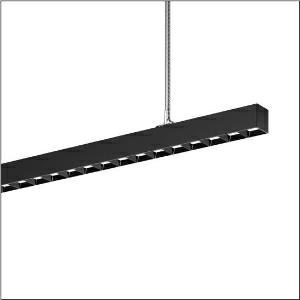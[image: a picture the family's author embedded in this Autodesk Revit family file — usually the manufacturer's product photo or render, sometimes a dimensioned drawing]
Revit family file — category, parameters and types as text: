
# Revit family: silica_r__21_51mx32dc3dbb_53cb
name_source: partatom
category: Lighting Fixtures
units: mm (PartAtom-declared; Revit-internal decimal feet)

## family parameters
Cut with Voids When Loaded = No
Host = Face
Light Source = No
Part Type = Normal
Room Calculation Point = No
Round Connector Dimension = Use Diameter
Shared = No

## types (1)
- --- (1 x LED, 18220 lm, 113 W, 3000K)
    Apparent Load = 113 VA
    CIE Flux Codes = 86 99 100 59 100
    Color Rendering = 80
    Color Temperature = 3000K
    Default Elevation = 1800 mm
    Description = Silica® 21, office luminaire, primary light control with darklight reflector, of PMMA, black, CAT 2 (L<= 3000cd/m²), light emission: direct/indirect distribution, primary light characteristic: symmetric, installation type: suspended mounting, LED, rated luminous flux: 18.220lm, luminous efficacy: 161lm/W, light colour: 830, colour temperature: 3000K, with terminal, 3+2-pole, max. 2.5mm², mains connection: 220..240V, AC, 50/60Hz, rated input power: 113W, luminaire housing, of aluminium, jet black (RAL 9005), length: 3.004mm, width: 53mm, height: 53mm, protection rating (complete): IP20, insulation class (complete): insulation class I (protective earthing), certification: CE, permissible operating ambient temperature: 0..+35°C, standard: EN 50419, packaging unit: 1 piece
    Height = 53 mm
    Lamp = 1 x LED
    Lamp Light Flux = 18220 lm
    Lamp Power = 113 W
    Lamp count = 1
    Length = 3004 mm
    Luminous efficacy = 161 lm/W
    Manufacturer = Siteco
    ModVariant = No
    Model = 51MX32DC3DBB
    Mounting Place = Ceiling
    Mounting Type = Pendant
    Number of Poles = 1
    OnlyDefault = Yes
    Power Factor = 1
    Product Name = Silica® 21
    Product group = office luminaire | ceiling pendant
    ProductGroupID = 902
    Protection Class = Protection class I
    Protection Degree = IP 20
    RLX_Detail_Level = 1
    RLX_Emergency_Light_Flux = 0 lm
    RLX_Emergency_Type = 0
    RLX_Emergency_Type_DB = No
    RlxData = <blob elided: 66513 chars, md5=03dd7351>
    Socket = socket
    Standby Power = 0 W
    System Light Flux = 18220 lm
    System Power = 113 W
    Type Comments = factory setting: luminous flux: 100 % | dim-lin: 254 | 391 mA
    Type Image = l_1335852.jpg
    URL = http://relux.com
    VarID = @adj_091571
    Voltage = 0 V
    Weight = 0.00 kg
    Width = 53 mm

## geometry (parser evidence)
native form markers: Blend x4, Sweep x13
no freeform markers — native parametric forms only
